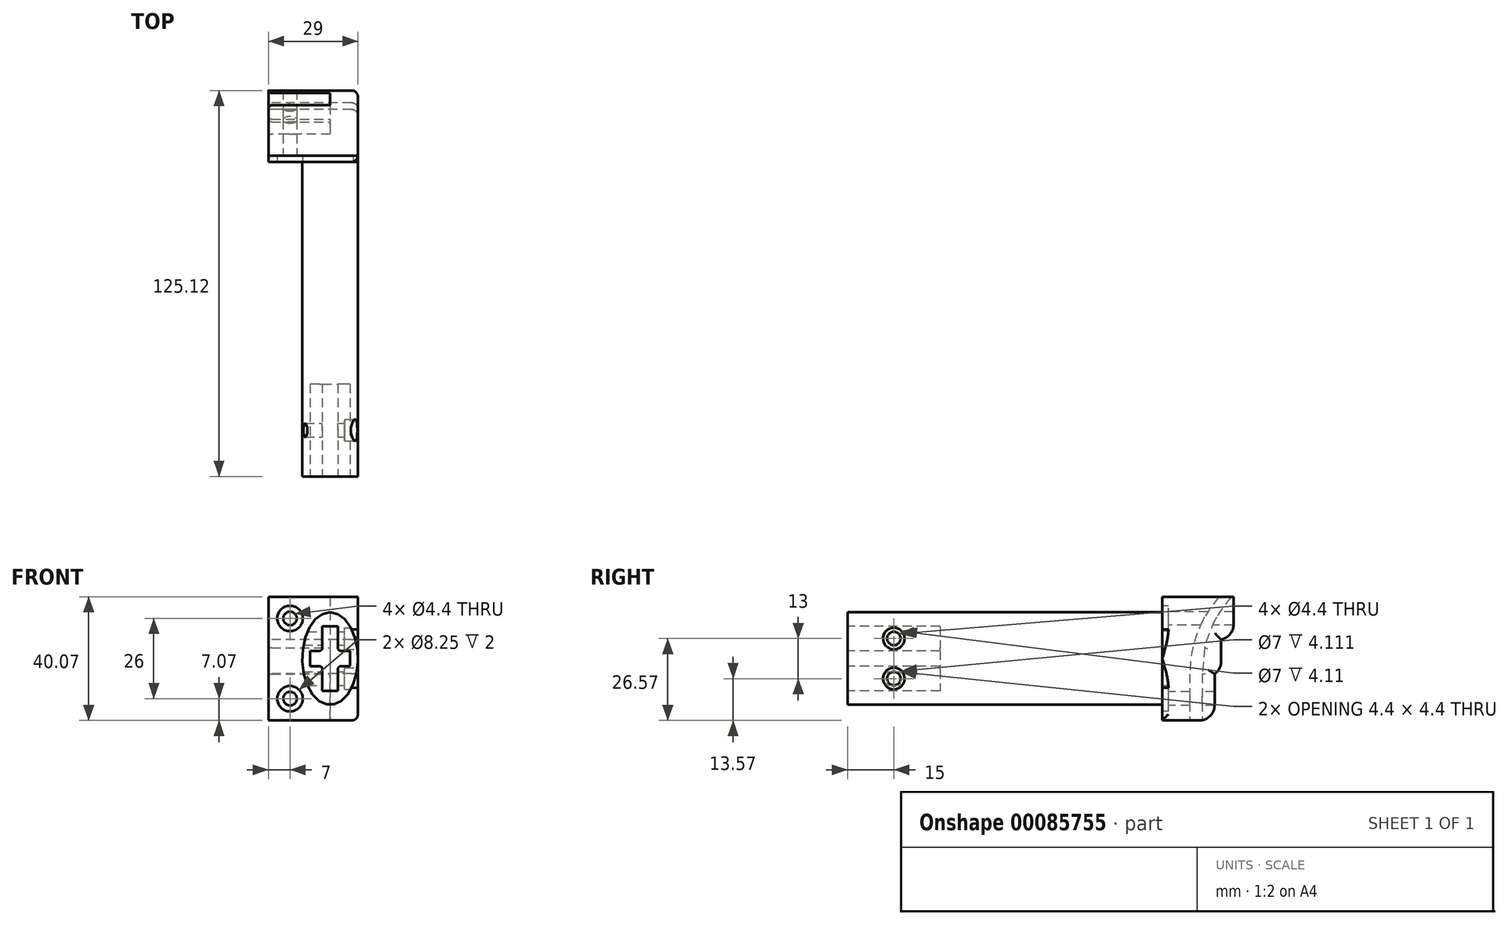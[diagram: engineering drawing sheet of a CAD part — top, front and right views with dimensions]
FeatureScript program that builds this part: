
annotation { "Feature Type Name" : "Feature", "Feature Type Description" : "" }
export const myFeature = defineFeature(function(context is Context, id is Id, definition is map)
    precondition{}
    {
        {
            var Q0;
            Q0=qCreatedBy(makeId("Front.planeOp"),FACE);
            var sketch = newSketch(context, id + "F0", { "sketchPlane" : qUnion([Q0])});
            skLineSegment(sketch, "E0.bottom", {"start": v(20, -20) * mm, "end": v(-20, -20) * mm});
            skLineSegment(sketch, "E0.top", {"start": v(20, 20) * mm, "end": v(-20, 20) * mm});
            skLineSegment(sketch, "E0.left", {"start": v(20, -20) * mm, "end": v(20, 20) * mm});
            skLineSegment(sketch, "E0.right", {"start": v(-20, -20) * mm, "end": v(-20, 20) * mm});
            skSolve(sketch);
        }
        {
            var Q0;
            Q0=makeQuery(id+"F0.imprint","IMPRINT",FACE,{"disambiguationData":[TD([[makeQuery(id+"F0.imprint","IMPRINT",EDGE,{"derivedFrom":sQuery(id+"F0.wireOp",EDGE,"E0.bottom")}),-1.0]])]});
            var sketch = newSketch(context, id + "F1", { "sketchPlane" : qUnion([Q0])});
            skEllipse(sketch, "E1", {"center": v(0, 0) * mm, "majorRadius": 15 * mm, "minorRadius": 9 * mm, "majorAxis": v(0, 1)});
            skPoint(sketch, "E2", {"position": v(-9, 0) * mm});
            skPoint(sketch, "E3", {"position": v(0, 15) * mm});
            skPoint(sketch, "E4", {"position": v(9, 0) * mm});
            skSolve(sketch);
        }
        {
            var Q0;
            Q0=qCreatedBy(makeId("Front.planeOp"),FACE);
            var sketch = newSketch(context, id + "F2", { "sketchPlane" : qUnion([Q0])});
            skCircle(sketch, "E5", {"center": v(-13, 13) * mm, "radius": 1.75 * mm});
            skCircle(sketch, "E6.MirrorC", {"center": v(13, 13) * mm, "radius": 1.75 * mm});
            skCircle(sketch, "E7.MirrorC", {"center": v(13, -13) * mm, "radius": 1.75 * mm});
            skCircle(sketch, "E8.MirrorC", {"center": v(-13, -13) * mm, "radius": 1.75 * mm});
            skSolve(sketch);
        }
        {
            var Q0;
            Q0=qSketchRegion(id+"F0",true);
            extrude(context, id + "F3", {"entities" : qUnion([Q0]), "oppositeDirection" : true, "depth" : 4 * mm});
        }
        {
            var Q0;
            Q0=qSketchRegion(id+"F1",true);
            extrude(context, id + "F4", {"entities" : qUnion([Q0]), "operationType" : NewBodyOperationType.ADD, "depth" : 50 * mm});
        }
        {
            var Q0;
            Q0=makeQuery(id+"F4.opExtrude","CAP_FACE",FACE,{"disambiguationData":[OSD([sQuery(id+"F1.wireOp",EDGE,"E1")])],"isStart":false});
            extrude(context, id + "F5", {"entities" : qUnion([Q0]), "operationType" : NewBodyOperationType.ADD, "depth" : 50 * mm});
        }
        {
            var Q0;
            Q0=qCreatedBy(makeId("Right.planeOp"),FACE);
            var sketch = newSketch(context, id + "F6", { "sketchPlane" : qUnion([Q0])});
            skArc(sketch, "E9", {"start": v(20.34, 19.93) * mm, "mid": v(13.4, 8.32) * mm, "end": v(10.97, -4.99) * mm});
            skLineSegment(sketch, "E10.top", {"start": v(3.97, -20.07) * mm, "end": v(10.97, -20.07) * mm});
            skLineSegment(sketch, "E10.left", {"start": v(3.97, 19.93) * mm, "end": v(3.97, -20.07) * mm});
            skPoint(sketch, "E11", {"position": v(20.34, 19.93) * mm});
            skLineSegment(sketch, "E12", {"start": v(20.34, 19.93) * mm, "end": v(3.97, 19.93) * mm});
            skLineSegment(sketch, "E13", {"start": v(10.97, -4.99) * mm, "end": v(10.97, -20.07) * mm});
            skLineSegment(sketch, "E14", {"start": v(10.97, -4.99) * mm, "end": v(10.97, -4.99) * mm});
            skPoint(sketch, "E15.orphan", {"position": v(10.97, -5.06) * mm});
            skPoint(sketch, "E16.end.orphan", {"position": v(10.97, 43.1) * mm});
            skArc(sketch, "E17", {"start": v(27.86, 19.93) * mm, "mid": v(21.13, 7.87) * mm, "end": v(18.97, -5.77) * mm});
            skLineSegment(sketch, "E18", {"start": v(20.34, 19.93) * mm, "end": v(22.78, 19.93) * mm});
            skLineSegment(sketch, "E19", {"start": v(27.86, 19.93) * mm, "end": v(22.78, 19.93) * mm});
            skLineSegment(sketch, "E20", {"start": v(18.97, -5.77) * mm, "end": v(19.25, -20.07) * mm});
            skLineSegment(sketch, "E21", {"start": v(19.25, -20.07) * mm, "end": v(10.97, -20.07) * mm});
            skSolve(sketch);
        }
        {
            var Q0;
            Q0=makeQuery(id+"F6.imprint","IMPRINT",FACE,{"disambiguationData":[TD([[makeQuery(id+"F6.imprint","IMPRINT",EDGE,{"derivedFrom":sQuery(id+"F6.wireOp",EDGE,"b2e3a52c-6a2f-4f61-9776-4fb108e23117")}),-1.0]])]});
            var Q1;
            Q1=makeQuery(id+"F6.imprint","IMPRINT",FACE,{"disambiguationData":[TD([[makeQuery(id+"F6.imprint","IMPRINT",EDGE,{"derivedFrom":sQuery(id+"F6.wireOp",EDGE,"E9")}),-1.0]])]});
            extrude(context, id + "F7", {"entities" : qUnion([Q0, Q1]), "operationType" : NewBodyOperationType.ADD, "endBound" : BoundingType.SYMMETRIC, "oppositeDirection" : true, "depth" : 40 * mm, "hasDraft" : true, "draftAngle" : 0 * degree});
        }
        {
            var Q0;
            Q0=makeQuery(id+"F3.opExtrude","CAP_FACE",FACE,{"disambiguationData":[OSD([sQuery(id+"F0.wireOp",EDGE,"E0.bottom"),sQuery(id+"F0.wireOp",EDGE,"E0.top"),sQuery(id+"F0.wireOp",EDGE,"E0.left"),sQuery(id+"F0.wireOp",EDGE,"E0.right")])],"isStart":true});
            extrude(context, id + "F8", {"entities" : qUnion([Q0]), "operationType" : NewBodyOperationType.REMOVE, "oppositeDirection" : true, "depth" : 2 * mm});
        }
        {
            var Q0;
            Q0=qCreatedBy(makeId("Right.planeOp"),FACE);
            var sketch = newSketch(context, id + "F9", { "sketchPlane" : qUnion([Q0])});
            skArc(sketch, "E22", {"start": v(20.34, 19.93) * mm, "mid": v(13.25, 8.36) * mm, "end": v(10.97, -5.01) * mm});
            skLineSegment(sketch, "E23", {"start": v(10.97, -4.87) * mm, "end": v(10.97, -20.07) * mm});
            skLineSegment(sketch, "E24", {"start": v(20.34, 19.93) * mm, "end": v(25.12, 19.93) * mm});
            skPoint(sketch, "E25.start.orphan", {"position": v(18.98, -5.36) * mm});
            skLineSegment(sketch, "E26", {"start": v(25.12, 19.93) * mm, "end": v(25.12, 6.17) * mm});
            skLineSegment(sketch, "E27", {"start": v(25.12, 6.17) * mm, "end": v(21.12, 6.17) * mm});
            skLineSegment(sketch, "E28", {"start": v(21.12, 6.17) * mm, "end": v(21.12, -4.93) * mm});
            skLineSegment(sketch, "E29", {"start": v(21.12, -4.93) * mm, "end": v(18.98, -4.93) * mm});
            skLineSegment(sketch, "E30", {"start": v(18.98, -4.93) * mm, "end": v(18.98, -20.07) * mm});
            skLineSegment(sketch, "E31", {"start": v(18.98, -20.07) * mm, "end": v(10.97, -20.07) * mm});
            skSolve(sketch);
        }
        {
            var Q0;
            Q0=qCreatedBy(makeId("Right.planeOp"),FACE);
            var sketch = newSketch(context, id + "F10", { "sketchPlane" : qUnion([Q0])});
            skArc(sketch, "E32", {"start": v(24.34, 19.93) * mm, "mid": v(19.02, 12.2) * mm, "end": v(15.75, 3.42) * mm});
            skLineSegment(sketch, "E33", {"start": v(14.97, -4.99) * mm, "end": v(14.97, -20.07) * mm});
            skLineSegment(sketch, "E34", {"start": v(18.98, -20.07) * mm, "end": v(14.97, -20.07) * mm});
            skLineSegment(sketch, "E35", {"start": v(15.75, 3.42) * mm, "end": v(14.97, -4.99) * mm});
            skLineSegment(sketch, "E36", {"start": v(18.98, -20.07) * mm, "end": v(18.98, -4.93) * mm});
            skLineSegment(sketch, "E37", {"start": v(18.98, -4.93) * mm, "end": v(21.12, -4.93) * mm});
            skLineSegment(sketch, "E38", {"start": v(21.12, -4.93) * mm, "end": v(21.12, 6.17) * mm});
            skLineSegment(sketch, "E39", {"start": v(21.12, 6.17) * mm, "end": v(25.12, 6.17) * mm});
            skLineSegment(sketch, "E40", {"start": v(25.12, 6.17) * mm, "end": v(25.12, 19.93) * mm});
            skLineSegment(sketch, "E41", {"start": v(25.12, 19.93) * mm, "end": v(24.34, 19.93) * mm});
            skSolve(sketch);
        }
        {
            var Q0;
            Q0 = qSketchRegion(id + "F9", true);
            extrude(context, id + "F11", {"entities" : qUnion([Q0]), "operationType" : NewBodyOperationType.ADD, "depth" : 9 * mm});
        }
        {
            var Q0;
            Q0 = qSketchRegion(id + "F10", true);
            extrude(context, id + "F12", {"entities" : qUnion([Q0]), "operationType" : NewBodyOperationType.ADD, "oppositeDirection" : true, "depth" : 20 * mm});
        }
        {
            var Q0;
            Q0=sQuery(id+"F2.wireOp",VERTEX,"E5.center");
            var Q1;
            Q1=sQuery(id+"F2.wireOp",VERTEX,"E8.MirrorC.center");
            var Q2;
            Q2=makeQuery(id+"F3.opExtrude","SWEPT_BODY",BODY,{"disambiguationData":[OSD([sQuery(id+"F0.wireOp",EDGE,"E0.bottom"),sQuery(id+"F0.wireOp",EDGE,"E0.top"),sQuery(id+"F0.wireOp",EDGE,"E0.left"),sQuery(id+"F0.wireOp",EDGE,"E0.right")])]});
            var Q3;
            Q3=makeQuery(id+"F7.split0.splitOp","SPLIT",BODY,{"derivedFrom":makeQuery(id+"F7.opExtrude","SWEPT_BODY",BODY,{"disambiguationData":[OSD([sQuery(id+"F6.wireOp",EDGE,"E9"),sQuery(id+"F6.wireOp",EDGE,"E10.top"),sQuery(id+"F6.wireOp",EDGE,"E10.left"),sQuery(id+"F6.wireOp",EDGE,"E12"),sQuery(id+"F6.wireOp",EDGE,"E13")])]})});
            var Q4;
            Q4=makeQuery(id+"F12.opExtrude","SWEPT_BODY",BODY,{"disambiguationData":[OSD([sQuery(id+"F10.wireOp",EDGE,"E32"),sQuery(id+"F10.wireOp",EDGE,"E33"),sQuery(id+"F10.wireOp",EDGE,"8730604a-b371-4a65-8ac8-68d83ceac879"),sQuery(id+"F10.wireOp",EDGE,"913d1105-7598-44c8-aded-8feed08280e7"),sQuery(id+"F10.wireOp",EDGE,"dae9e258-54e4-4acf-b6be-6e3aee2d9672"),sQuery(id+"F10.wireOp",EDGE,"E34"),sQuery(id+"F10.wireOp",EDGE,"E35")])]});
            hole(context, id + "F13", {"style" : HoleStyle.C_BORE, "endStyle" : HoleEndStyle.BLIND, "standardTappedOrClearance" : lookupTablePath({ "standard" : "ISO", "fit" : "Normal", "size" : "M4", "type" : "Clearance" }), "standardBlindInLast" : lookupTablePath({ "fit" : "Standard", "standard" : "ISO", "size" : "M4", "type" : "Clearance" }), "holeDiameter" : 4.4 * mm, "cBoreDiameter" : 8.25 * mm, "cBoreDepth" : 4 * mm, "holeDepth" : 50 * mm, "startFromSketch" : true, "locations" : qUnion([Q0, Q1]), "scope" : qUnion([Q2, Q3, Q4])});
        }
        {
            var Q0;
            Q0=qCreatedBy(makeId("Right.planeOp"),FACE);
            cPlane(context, id + "F14", {"entities" : qUnion([Q0]), "cplaneType" : CPlaneType.OFFSET, "offset" : 14 * mm, "width" : 150 * mm, "height" : 150 * mm});
        }
        {
            var Q0;
            Q0=qCreatedBy(id+"F14.planeOp",FACE);
            var sketch = newSketch(context, id + "F15", { "sketchPlane" : qUnion([Q0])});
            skPoint(sketch, "E42", {"position": v(-85, 6.5) * mm});
            skPoint(sketch, "E43.MirrorP", {"position": v(-85, -6.5) * mm});
            skSolve(sketch);
        }
        {
            var Q0;
            Q0=sQuery(id+"F15.wireOp",VERTEX,"E42");
            var Q1;
            Q1=sQuery(id+"F15.wireOp",VERTEX,"E43.MirrorP");
            var Q2;
            Q2=makeQuery(id+"F3.opExtrude","SWEPT_BODY",BODY,{"disambiguationData":[OSD([sQuery(id+"F0.wireOp",EDGE,"E0.bottom"),sQuery(id+"F0.wireOp",EDGE,"E0.top"),sQuery(id+"F0.wireOp",EDGE,"E0.left"),sQuery(id+"F0.wireOp",EDGE,"E0.right")])]});
            hole(context, id + "F16", {"style" : HoleStyle.C_BORE, "endStyle" : HoleEndStyle.BLIND, "holeDiameter" : 4.4 * mm, "cBoreDiameter" : 7 * mm, "cBoreDepth" : 2 * mm, "holeDepth" : 30 * mm, "locations" : qUnion([Q0, Q1]), "scope" : qUnion([Q2])});
        }
        {
            var Q0;
            Q0=makeQuery(id+"F5.opExtrude","CAP_FACE",FACE,{"disambiguationData":[OSD([sQuery(id+"F1.wireOp",EDGE,"E1")])],"isStart":false});
            var sketch = newSketch(context, id + "F17", { "sketchPlane" : qUnion([Q0])});
            skLineSegment(sketch, "E44", {"start": v(0, 10.5) * mm, "end": v(2.5, 10.5) * mm});
            skLineSegment(sketch, "E45", {"start": v(2.5, 10.5) * mm, "end": v(2.5, 2.5) * mm});
            skLineSegment(sketch, "E46", {"start": v(2.5, 2.5) * mm, "end": v(6.5, 2.5) * mm});
            skLineSegment(sketch, "E47", {"start": v(6.5, 2.5) * mm, "end": v(6.5, -2.5) * mm});
            skLineSegment(sketch, "E48", {"start": v(6.5, -2.5) * mm, "end": v(2.5, -2.5) * mm});
            skLineSegment(sketch, "E49", {"start": v(2.5, -2.5) * mm, "end": v(2.5, -10.5) * mm});
            skLineSegment(sketch, "E50", {"start": v(2.5, -10.5) * mm, "end": v(0, -10.5) * mm});
            skLineSegment(sketch, "E51", {"start": v(0, 10.5) * mm, "end": v(-2.5, 10.5) * mm});
            skLineSegment(sketch, "E52", {"start": v(-2.5, 10.5) * mm, "end": v(-2.5, 2.5) * mm});
            skLineSegment(sketch, "E53", {"start": v(-2.5, 2.5) * mm, "end": v(-6.5, 2.5) * mm});
            skLineSegment(sketch, "E54", {"start": v(-6.5, 2.5) * mm, "end": v(-6.5, -2.5) * mm});
            skLineSegment(sketch, "E55", {"start": v(-6.5, -2.5) * mm, "end": v(-2.5, -2.5) * mm});
            skLineSegment(sketch, "E56", {"start": v(-2.5, -2.5) * mm, "end": v(-2.5, -10.5) * mm});
            skLineSegment(sketch, "E57", {"start": v(-2.5, -10.5) * mm, "end": v(0, -10.5) * mm});
            skSolve(sketch);
        }
        {
            var Q0;
            Q0=makeQuery(id+"F17.imprint","IMPRINT",FACE,{"disambiguationData":[TD([[makeQuery(id+"F17.imprint","IMPRINT",EDGE,{"derivedFrom":sQuery(id+"F17.wireOp",EDGE,"E44")}),-1.0]])]});
            extrude(context, id + "F18", {"entities" : qUnion([Q0]), "operationType" : NewBodyOperationType.REMOVE, "oppositeDirection" : true, "depth" : 30 * mm});
        }
        {
            var Q0;
            Q0=qCreatedBy(makeId("Front.planeOp"),FACE);
            var sketch = newSketch(context, id + "F19", { "sketchPlane" : qUnion([Q0])});
            skLineSegment(sketch, "E58.bottom", {"start": v(9, 21) * mm, "end": v(22.8, 21) * mm});
            skLineSegment(sketch, "E58.top", {"start": v(9, -21) * mm, "end": v(22.8, -21) * mm});
            skLineSegment(sketch, "E58.left", {"start": v(9, 21) * mm, "end": v(9, -21) * mm});
            skLineSegment(sketch, "E58.right", {"start": v(22.8, 21) * mm, "end": v(22.8, -21) * mm});
            skSolve(sketch);
        }
        {
            var Q0;
            Q0 = qSketchRegion(id + "F19", true);
            extrude(context, id + "F20", {"entities" : qUnion([Q0]), "operationType" : NewBodyOperationType.REMOVE, "oppositeDirection" : true, "depth" : 50 * mm});
        }
        {
            var Q0;
            Q0=makeQuery(id+"F12.opExtrude","SWEPT_EDGE",EDGE,{"disambiguationData":[OSD([sQuery(id+"F10.wireOp",EDGE,"E39"),sQuery(id+"F10.wireOp",EDGE,"E40")])]});
            var Q1;
            Q1=makeQuery(id+"F11.opExtrude","SWEPT_EDGE",EDGE,{"disambiguationData":[OSD([sQuery(id+"F9.wireOp",EDGE,"E26"),sQuery(id+"F9.wireOp",EDGE,"E27")])]});
            var Q2;
            Q2=makeQuery(id+"F12.opExtrude","SWEPT_EDGE",EDGE,{"disambiguationData":[OSD([sQuery(id+"F10.wireOp",EDGE,"E37"),sQuery(id+"F10.wireOp",EDGE,"E38")])]});
            var Q3;
            Q3=makeQuery(id+"F11.opExtrude","SWEPT_EDGE",EDGE,{"disambiguationData":[OSD([sQuery(id+"F9.wireOp",EDGE,"E28"),sQuery(id+"F9.wireOp",EDGE,"E29")])]});
            var Q4;
            Q4=makeQuery(id+"F12.opExtrude","SWEPT_EDGE",EDGE,{"disambiguationData":[OSD([sQuery(id+"F10.wireOp",EDGE,"E34"),sQuery(id+"F10.wireOp",EDGE,"E36")])]});
            var Q5;
            Q5=makeQuery(id+"F11.opExtrude","SWEPT_EDGE",EDGE,{"disambiguationData":[OSD([sQuery(id+"F9.wireOp",EDGE,"E30"),sQuery(id+"F9.wireOp",EDGE,"E31")])]});
            fillet(context, id + "F21", {"entities" : qUnion([Q0, Q1, Q2, Q3, Q4, Q5]), "radius" : 5 * mm, "tangentPropagation" : true, "allowEdgeOverflow" : false});
        }
        {
            var Q0;
            Q0=makeQuery(id+"F8.boolean.opBoolean","COPY",EDGE,{"derivedFrom":makeQuery(id+"F8.opExtrude","CAP_EDGE",EDGE,{"disambiguationData":[OSD([sQuery(id+"F0.wireOp",EDGE,"E0.bottom")])],"isStart":false})});
            var Q1;
            Q1=makeQuery(id+"F8.boolean.opBoolean","COPY",EDGE,{"derivedFrom":makeQuery(id+"F8.opExtrude","CAP_EDGE",EDGE,{"disambiguationData":[OSD([sQuery(id+"F0.wireOp",EDGE,"E0.top")])],"isStart":false})});
            var Q2;
            Q2=makeQuery(id+"F8.boolean.opBoolean","COPY",EDGE,{"derivedFrom":makeQuery(id+"F8.opExtrude","CAP_EDGE",EDGE,{"disambiguationData":[OSD([sQuery(id+"F0.wireOp",EDGE,"E0.right")])],"isStart":false})});
            var Q3;
            Q3=makeQuery(id+"F20.boolean.opBoolean","INTERSECT",EDGE,{"disambiguationData":[OD(1.0)],"derivedFrom":[makeQuery(id+"F8.boolean.opBoolean","COPY",FACE,{"derivedFrom":makeQuery(id+"F8.opExtrude","CAP_FACE",FACE,{"disambiguationData":[OSD([sQuery(id+"F0.wireOp",EDGE,"E0.bottom"),sQuery(id+"F0.wireOp",EDGE,"E0.top"),sQuery(id+"F0.wireOp",EDGE,"E0.left"),sQuery(id+"F0.wireOp",EDGE,"E0.right")])],"isStart":false})}),makeQuery(id+"F20.opExtrude","SWEPT_FACE",FACE,{"disambiguationData":[OSD([sQuery(id+"F19.wireOp",EDGE,"E58.left")])]})]});
            var Q4;
            Q4=makeQuery(id+"F20.boolean.opBoolean","INTERSECT",EDGE,{"disambiguationData":[OD(0.0)],"derivedFrom":[makeQuery(id+"F8.boolean.opBoolean","COPY",FACE,{"derivedFrom":makeQuery(id+"F8.opExtrude","CAP_FACE",FACE,{"disambiguationData":[OSD([sQuery(id+"F0.wireOp",EDGE,"E0.bottom"),sQuery(id+"F0.wireOp",EDGE,"E0.top"),sQuery(id+"F0.wireOp",EDGE,"E0.left"),sQuery(id+"F0.wireOp",EDGE,"E0.right")])],"isStart":false})}),makeQuery(id+"F20.opExtrude","SWEPT_FACE",FACE,{"disambiguationData":[OSD([sQuery(id+"F19.wireOp",EDGE,"E58.left")])]})]});
            var Q5;
            {var subQ0=makeQuery(id+"F7.opExtrude","SWEPT_FACE",FACE,{"disambiguationData":[OSD([sQuery(id+"F6.wireOp",EDGE,"E10.top")])]});Q5=makeQuery(id+"F20.boolean.opBoolean","INTERSECT",EDGE,{"derivedFrom":[makeQuery(id+"F7.booleanUnion0.opBoolean","MERGE",FACE,{"derivedFrom":[makeQuery(id+"F7.split0.splitOp","SPLIT",FACE,{"derivedFrom":subQ0}),makeQuery(id+"F7.split0.splitOp","SPLIT",FACE,{"derivedFrom":subQ0,"isFromBackBody":true})]}),makeQuery(id+"F20.opExtrude","SWEPT_FACE",FACE,{"disambiguationData":[OSD([sQuery(id+"F19.wireOp",EDGE,"E58.left")])]})]});}
            var Q6;
            Q6=makeQuery(id+"F11.opExtrude","CAP_EDGE",EDGE,{"disambiguationData":[OSD([sQuery(id+"F9.wireOp",EDGE,"E31")])],"isStart":false});
            var Q7;
            {var subQ0=sQuery(id+"F9.wireOp",EDGE,"E29");var subQ1=sQuery(id+"F9.wireOp",EDGE,"E28");Q7=makeQuery(id+"F21.opFillet","BLEND_EDGE",EDGE,{"blendedFrom":[makeQuery(id+"F11.opExtrude","SWEPT_EDGE",EDGE,{"disambiguationData":[OSD([subQ1,subQ0])]}),makeQuery(id+"F11.opExtrude","CAP_FACE",FACE,{"disambiguationData":[OSD([sQuery(id+"F9.wireOp",EDGE,"E22"),sQuery(id+"F9.wireOp",EDGE,"E23"),sQuery(id+"F9.wireOp",EDGE,"E24"),sQuery(id+"F9.wireOp",EDGE,"E26"),sQuery(id+"F9.wireOp",EDGE,"E27"),subQ1,subQ0,sQuery(id+"F9.wireOp",EDGE,"E30"),sQuery(id+"F9.wireOp",EDGE,"E31")])],"isStart":false})],"blendedInto":[makeQuery(id+"F11.opExtrude","CAP_FACE",FACE,{"disambiguationData":[OSD([sQuery(id+"F9.wireOp",EDGE,"E22"),sQuery(id+"F9.wireOp",EDGE,"E23"),sQuery(id+"F9.wireOp",EDGE,"E24"),sQuery(id+"F9.wireOp",EDGE,"E26"),sQuery(id+"F9.wireOp",EDGE,"E27"),subQ1,subQ0,sQuery(id+"F9.wireOp",EDGE,"E30"),sQuery(id+"F9.wireOp",EDGE,"E31")])],"isStart":false})]});}
            var Q8;
            {var subQ0=sQuery(id+"F9.wireOp",EDGE,"E27");var subQ1=sQuery(id+"F9.wireOp",EDGE,"E26");Q8=makeQuery(id+"F21.opFillet","BLEND_EDGE",EDGE,{"blendedFrom":[makeQuery(id+"F11.opExtrude","SWEPT_EDGE",EDGE,{"disambiguationData":[OSD([subQ1,subQ0])]}),makeQuery(id+"F11.opExtrude","CAP_FACE",FACE,{"disambiguationData":[OSD([sQuery(id+"F9.wireOp",EDGE,"E22"),sQuery(id+"F9.wireOp",EDGE,"E23"),sQuery(id+"F9.wireOp",EDGE,"E24"),subQ1,subQ0,sQuery(id+"F9.wireOp",EDGE,"E28"),sQuery(id+"F9.wireOp",EDGE,"E29"),sQuery(id+"F9.wireOp",EDGE,"E30"),sQuery(id+"F9.wireOp",EDGE,"E31")])],"isStart":false})],"blendedInto":[makeQuery(id+"F11.opExtrude","CAP_FACE",FACE,{"disambiguationData":[OSD([sQuery(id+"F9.wireOp",EDGE,"E22"),sQuery(id+"F9.wireOp",EDGE,"E23"),sQuery(id+"F9.wireOp",EDGE,"E24"),subQ1,subQ0,sQuery(id+"F9.wireOp",EDGE,"E28"),sQuery(id+"F9.wireOp",EDGE,"E29"),sQuery(id+"F9.wireOp",EDGE,"E30"),sQuery(id+"F9.wireOp",EDGE,"E31")])],"isStart":false})]});}
            var Q9;
            Q9=makeQuery(id+"F11.opExtrude","CAP_EDGE",EDGE,{"disambiguationData":[OSD([sQuery(id+"F9.wireOp",EDGE,"E24")])],"isStart":false});
            fillet(context, id + "F22", {"entities" : qUnion([Q0, Q1, Q2, Q3, Q4, Q5, Q6, Q7, Q8, Q9]), "radius" : 2 * mm, "tangentPropagation" : true, "allowEdgeOverflow" : false});
        }
        {
            var Q0;
            Q0=makeQuery(id+"F7.opExtrude","CAP_EDGE",EDGE,{"disambiguationData":[OSD([sQuery(id+"F6.wireOp",EDGE,"E9")])],"isStart":false});
            var Q1;
            Q1=makeQuery(id+"F7.opExtrude","CAP_EDGE",EDGE,{"disambiguationData":[OSD([sQuery(id+"F6.wireOp",EDGE,"E13")])],"isStart":false});
            var Q2;
            Q2=makeQuery(id+"F12.opExtrude","CAP_EDGE",EDGE,{"disambiguationData":[OSD([sQuery(id+"F10.wireOp",EDGE,"E33")])],"isStart":false});
            var Q3;
            Q3=makeQuery(id+"F12.opExtrude","CAP_EDGE",EDGE,{"disambiguationData":[OSD([sQuery(id+"F10.wireOp",EDGE,"E35")])],"isStart":false});
            var Q4;
            Q4=makeQuery(id+"F12.opExtrude","CAP_EDGE",EDGE,{"disambiguationData":[OSD([sQuery(id+"F10.wireOp",EDGE,"E32")])],"isStart":false});
            fillet(context, id + "F23", {"entities" : qUnion([Q0, Q1, Q2, Q3, Q4]), "radius" : 1 * mm, "tangentPropagation" : true, "allowEdgeOverflow" : false});
        }
        {
            var Q0;
            Q0=makeQuery(id+"F18.boolean.opBoolean","COPY",EDGE,{"derivedFrom":makeQuery(id+"F18.opExtrude","CAP_EDGE",EDGE,{"disambiguationData":[OSD([sQuery(id+"F17.wireOp",EDGE,"E52")])],"isStart":true})});
            var Q1;
            Q1=makeQuery(id+"F18.boolean.opBoolean","COPY",EDGE,{"derivedFrom":makeQuery(id+"F18.opExtrude","CAP_EDGE",EDGE,{"disambiguationData":[OSD([sQuery(id+"F17.wireOp",EDGE,"E53")])],"isStart":true})});
            var Q2;
            Q2=makeQuery(id+"F18.boolean.opBoolean","COPY",EDGE,{"derivedFrom":makeQuery(id+"F18.opExtrude","CAP_EDGE",EDGE,{"disambiguationData":[OSD([sQuery(id+"F17.wireOp",EDGE,"E54")])],"isStart":true})});
            var Q3;
            Q3=makeQuery(id+"F18.boolean.opBoolean","COPY",EDGE,{"derivedFrom":makeQuery(id+"F18.opExtrude","CAP_EDGE",EDGE,{"disambiguationData":[OSD([sQuery(id+"F17.wireOp",EDGE,"E55")])],"isStart":true})});
            var Q4;
            Q4=makeQuery(id+"F18.boolean.opBoolean","COPY",EDGE,{"derivedFrom":makeQuery(id+"F18.opExtrude","CAP_EDGE",EDGE,{"disambiguationData":[OSD([sQuery(id+"F17.wireOp",EDGE,"E56")])],"isStart":true})});
            var Q5;
            Q5=makeQuery(id+"F18.boolean.opBoolean","COPY",EDGE,{"derivedFrom":makeQuery(id+"F18.opExtrude","CAP_EDGE",EDGE,{"disambiguationData":[OSD([sQuery(id+"F17.wireOp",EDGE,"E50"),sQuery(id+"F17.wireOp",EDGE,"E57")])],"isStart":true})});
            var Q6;
            Q6=makeQuery(id+"F18.boolean.opBoolean","COPY",EDGE,{"derivedFrom":makeQuery(id+"F18.opExtrude","CAP_EDGE",EDGE,{"disambiguationData":[OSD([sQuery(id+"F17.wireOp",EDGE,"E49")])],"isStart":true})});
            var Q7;
            Q7=makeQuery(id+"F18.boolean.opBoolean","COPY",EDGE,{"derivedFrom":makeQuery(id+"F18.opExtrude","CAP_EDGE",EDGE,{"disambiguationData":[OSD([sQuery(id+"F17.wireOp",EDGE,"E48")])],"isStart":true})});
            var Q8;
            Q8=makeQuery(id+"F18.boolean.opBoolean","COPY",EDGE,{"derivedFrom":makeQuery(id+"F18.opExtrude","CAP_EDGE",EDGE,{"disambiguationData":[OSD([sQuery(id+"F17.wireOp",EDGE,"E47")])],"isStart":true})});
            var Q9;
            Q9=makeQuery(id+"F18.boolean.opBoolean","COPY",EDGE,{"derivedFrom":makeQuery(id+"F18.opExtrude","CAP_EDGE",EDGE,{"disambiguationData":[OSD([sQuery(id+"F17.wireOp",EDGE,"E46")])],"isStart":true})});
            var Q10;
            Q10=makeQuery(id+"F18.boolean.opBoolean","COPY",EDGE,{"derivedFrom":makeQuery(id+"F18.opExtrude","CAP_EDGE",EDGE,{"disambiguationData":[OSD([sQuery(id+"F17.wireOp",EDGE,"E45")])],"isStart":true})});
            var Q11;
            Q11=makeQuery(id+"F18.boolean.opBoolean","COPY",EDGE,{"derivedFrom":makeQuery(id+"F18.opExtrude","CAP_EDGE",EDGE,{"disambiguationData":[OSD([sQuery(id+"F17.wireOp",EDGE,"E44"),sQuery(id+"F17.wireOp",EDGE,"E51")])],"isStart":true})});
            var Q12;
            Q12=makeQuery(id+"F18.boolean.opBoolean","COPY",EDGE,{"derivedFrom":makeQuery(id+"F18.opExtrude","SWEPT_EDGE",EDGE,{"disambiguationData":[OSD([sQuery(id+"F17.wireOp",EDGE,"E52"),sQuery(id+"F17.wireOp",EDGE,"E53")])]})});
            var Q13;
            Q13=makeQuery(id+"F18.boolean.opBoolean","COPY",EDGE,{"derivedFrom":makeQuery(id+"F18.opExtrude","SWEPT_EDGE",EDGE,{"disambiguationData":[OSD([sQuery(id+"F17.wireOp",EDGE,"E45"),sQuery(id+"F17.wireOp",EDGE,"E46")])]})});
            var Q14;
            Q14=makeQuery(id+"F18.boolean.opBoolean","COPY",EDGE,{"derivedFrom":makeQuery(id+"F18.opExtrude","SWEPT_EDGE",EDGE,{"disambiguationData":[OSD([sQuery(id+"F17.wireOp",EDGE,"E55"),sQuery(id+"F17.wireOp",EDGE,"E56")])]})});
            var Q15;
            Q15=makeQuery(id+"F18.boolean.opBoolean","COPY",EDGE,{"derivedFrom":makeQuery(id+"F18.opExtrude","SWEPT_EDGE",EDGE,{"disambiguationData":[OSD([sQuery(id+"F17.wireOp",EDGE,"E48"),sQuery(id+"F17.wireOp",EDGE,"E49")])]})});
            fillet(context, id + "F24", {"entities" : qUnion([Q0, Q1, Q2, Q3, Q4, Q5, Q6, Q7, Q8, Q9, Q10, Q11, Q12, Q13, Q14, Q15]), "radius" : 1 * mm, "tangentPropagation" : true, "allowEdgeOverflow" : false});
        }
    });
